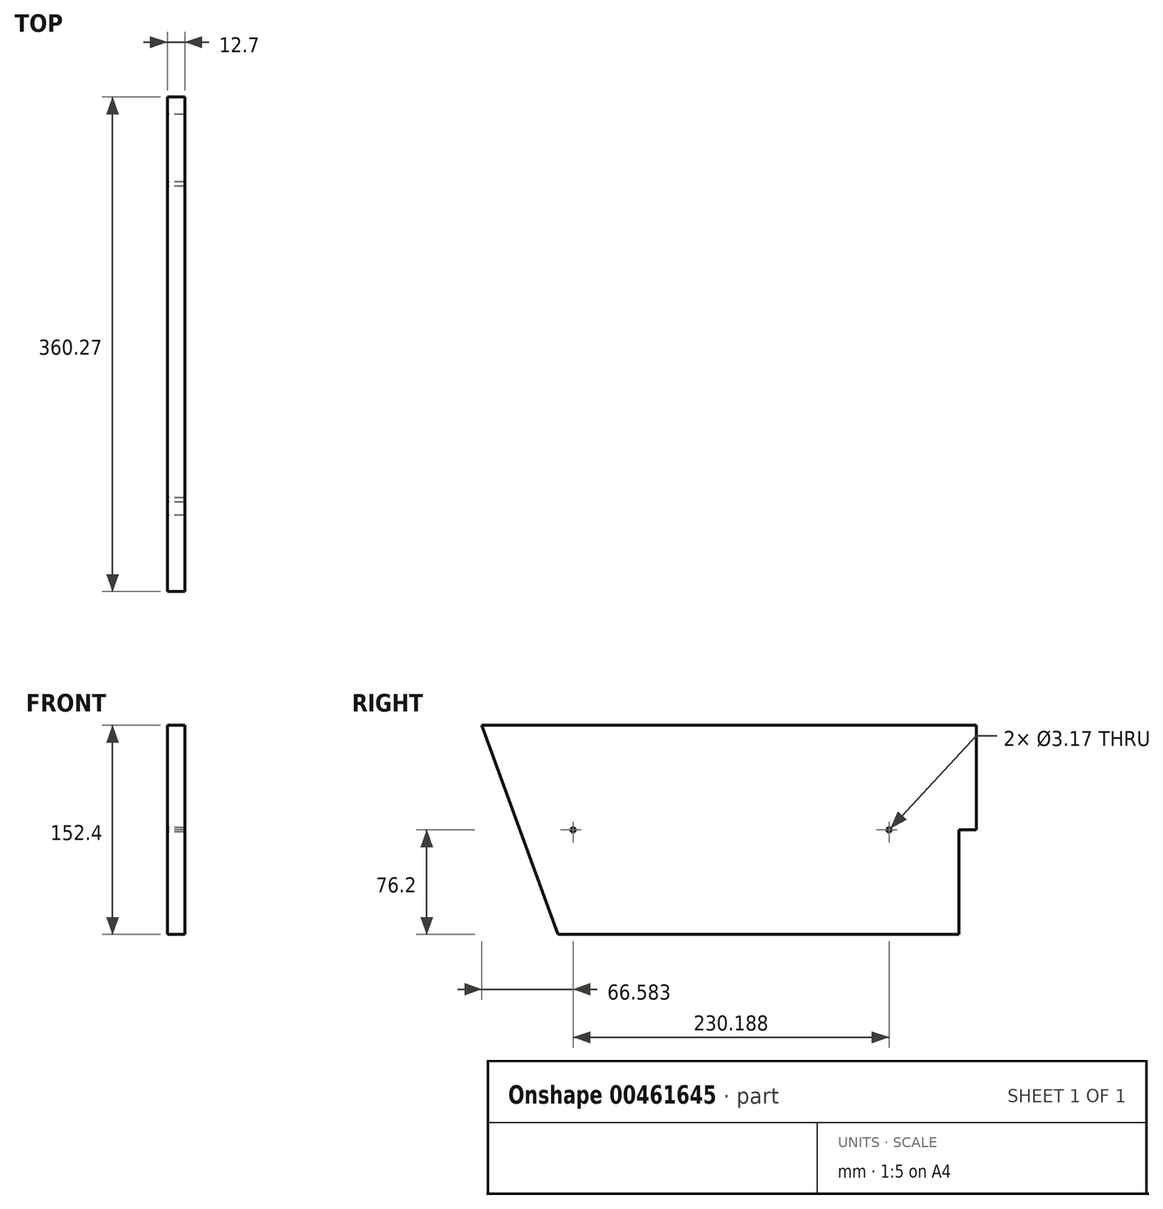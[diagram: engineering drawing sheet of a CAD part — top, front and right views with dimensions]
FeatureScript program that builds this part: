
annotation { "Feature Type Name" : "Feature", "Feature Type Description" : "" }
export const myFeature = defineFeature(function(context is Context, id is Id, definition is map)
    precondition{}
    {
        {
            var Q0;
            Q0=qCreatedBy(makeId("Right.planeOp"),FACE);
            var sketch = newSketch(context, id + "F0", { "sketchPlane" : qUnion([Q0])});
            skLineSegment(sketch, "E0.bottom", {"start": v(152.4, 76.2) * mm, "end": v(-152.4, 76.2) * mm});
            skLineSegment(sketch, "E0.top", {"start": v(152.4, -76.2) * mm, "end": v(-152.4, -76.2) * mm});
            skLineSegment(sketch, "E0.left", {"start": v(152.4, 76.2) * mm, "end": v(152.4, -76.2) * mm});
            skPoint(sketch, "E0.middle", {"position": v(0, 0) * mm});
            skLineSegment(sketch, "E1", {"start": v(-152.4, -76.2) * mm, "end": v(-207.87, 76.2) * mm});
            skLineSegment(sketch, "E2", {"start": v(-207.87, 76.2) * mm, "end": v(152.4, 76.2) * mm});
            skSolve(sketch);
        }
        {
            var Q0;
            Q0=makeQuery(id+"F0.imprint","IMPRINT",FACE,{"disambiguationData":[TD([[makeQuery(id+"F0.imprint","IMPRINT",EDGE,{"derivedFrom":sQuery(id+"F0.wireOp",EDGE,"E0.top")}),-1.0]])]});
            var sketch = newSketch(context, id + "F1", { "sketchPlane" : qUnion([Q0])});
            skLineSegment(sketch, "E3.bottom", {"start": v(152.4, -76.2) * mm, "end": v(139.7, -76.2) * mm});
            skLineSegment(sketch, "E3.top", {"start": v(152.4, 0) * mm, "end": v(139.7, 0) * mm});
            skLineSegment(sketch, "E3.left", {"start": v(152.4, -76.2) * mm, "end": v(152.4, 0) * mm});
            skLineSegment(sketch, "E3.right", {"start": v(139.7, -76.2) * mm, "end": v(139.7, 0) * mm});
            skSolve(sketch);
        }
        {
            var Q0;
            {var subQ5=sQuery(id+"F1.wireOp",EDGE,"E3.top");Q0=makeQuery(id+"F1.imprint","IMPRINT",FACE,{"disambiguationData":[TD([[makeQuery(id+"F1.imprint","IMPRINT",EDGE,{"derivedFrom":subQ5}),-1.0]])]});}
            var Q1;
            {var subQ0=sQuery(id+"F0.wireOp",EDGE,"E0.right");Q1=makeQuery(id+"F0.imprint","IMPRINT",FACE,{"disambiguationData":[TD([[makeQuery(id+"F0.imprint","IMPRINT",EDGE,{"derivedFrom":subQ0}),-1.0]])]});}
            extrude(context, id + "F2", {"entities" : qUnion([Q0, Q1]), "depth" : 12.7 * mm});
        }
        {
            var Q0;
            Q0=makeQuery(id+"F0.imprint","IMPRINT",FACE,{"disambiguationData":[TD([[makeQuery(id+"F0.imprint","IMPRINT",EDGE,{"derivedFrom":sQuery(id+"F0.wireOp",EDGE,"E0.top")}),-1.0]])]});
            var sketch = newSketch(context, id + "F3", { "sketchPlane" : qUnion([Q0])});
            skCircle(sketch, "E4", {"center": v(-141.29, 0) * mm, "radius": 1.59 * mm});
            skCircle(sketch, "E5", {"center": v(88.9, 0) * mm, "radius": 1.59 * mm});
            skSolve(sketch);
        }
        {
            var Q0;
            Q0 = qSketchRegion(id + "F3", true);
            extrude(context, id + "F4", {"entities" : qUnion([Q0]), "operationType" : NewBodyOperationType.REMOVE, "endBound" : BoundingType.THROUGH_ALL, "depth" : 25.4 * mm});
        }
    });
